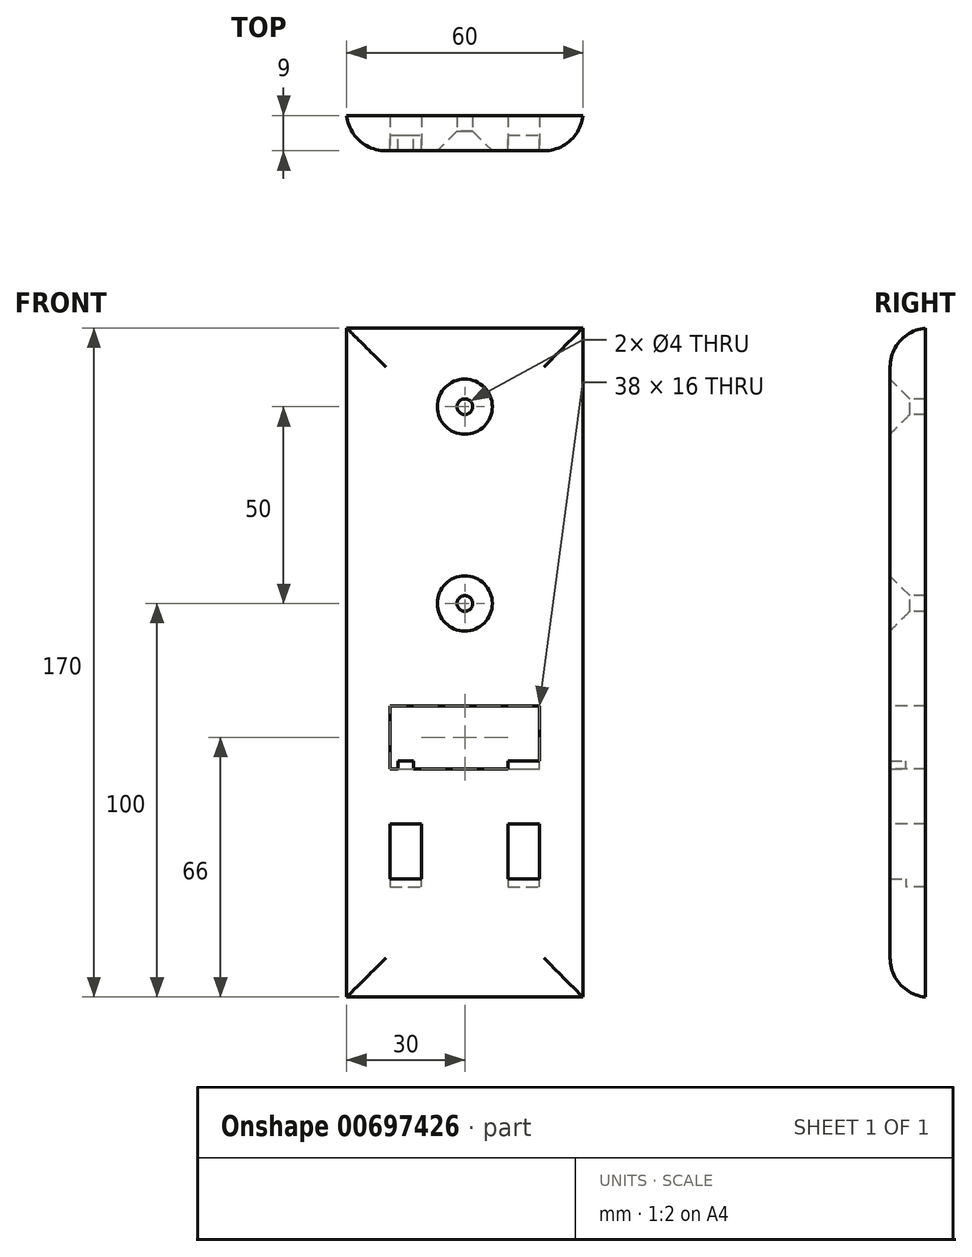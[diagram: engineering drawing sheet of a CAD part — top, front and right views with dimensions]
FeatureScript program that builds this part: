
annotation { "Feature Type Name" : "Feature", "Feature Type Description" : "" }
export const myFeature = defineFeature(function(context is Context, id is Id, definition is map)
    precondition{}
    {
        {
            var Q0;
            Q0=qCreatedBy(makeId("Front.planeOp"),FACE);
            var sketch = newSketch(context, id + "F0", { "sketchPlane" : qUnion([Q0])});
            skLineSegment(sketch, "E0", {"start": v(0, 0) * mm, "end": v(-30, 0) * mm});
            skLineSegment(sketch, "E1", {"start": v(-30, 0) * mm, "end": v(30, 0) * mm});
            skLineSegment(sketch, "E2", {"start": v(30, 0) * mm, "end": v(30, 80) * mm});
            skLineSegment(sketch, "E3", {"start": v(30, 80) * mm, "end": v(-30, 80) * mm});
            skLineSegment(sketch, "E4", {"start": v(-30, 80) * mm, "end": v(-30, 0) * mm});
            skLineSegment(sketch, "E5", {"start": v(-30, 0) * mm, "end": v(-30, 50) * mm, "construction": true});
            skLineSegment(sketch, "E6", {"start": v(-30, 50) * mm, "end": v(30, 50) * mm, "construction": true});
            skLineSegment(sketch, "E7", {"start": v(30, 50) * mm, "end": v(0, 50) * mm, "construction": true});
            skLineSegment(sketch, "E8", {"start": v(0, 50) * mm, "end": v(0, 20) * mm, "construction": true});
            skLineSegment(sketch, "E9", {"start": v(0, 20) * mm, "end": v(30, 20) * mm, "construction": true});
            skLineSegment(sketch, "E10", {"start": v(30, 20) * mm, "end": v(-30, 20) * mm, "construction": true});
            skPoint(sketch, "E10.endSnap0", {"position": v(15, 20) * mm});
            skLineSegment(sketch, "E11.bottom", {"start": v(15, 50) * mm, "end": v(-15, 50) * mm, "construction": true});
            skLineSegment(sketch, "E11.top", {"start": v(15, 20) * mm, "end": v(-15, 20) * mm, "construction": true});
            skLineSegment(sketch, "E11.left", {"start": v(15, 50) * mm, "end": v(15, 20) * mm, "construction": true});
            skLineSegment(sketch, "E11.right", {"start": v(-15, 50) * mm, "end": v(-15, 20) * mm, "construction": true});
            skPoint(sketch, "E11.middle", {"position": v(0, 35) * mm});
            skLineSegment(sketch, "E12", {"start": v(-15, 50) * mm, "end": v(15, 20) * mm, "construction": true});
            skLineSegment(sketch, "E13", {"start": v(15, 50) * mm, "end": v(-15, 20) * mm, "construction": true});
            skLineSegment(sketch, "E14.bottom", {"start": v(-11, 46) * mm, "end": v(-19, 46) * mm});
            skLineSegment(sketch, "E14.top", {"start": v(-11, 54) * mm, "end": v(-19, 54) * mm});
            skLineSegment(sketch, "E14.left", {"start": v(-11, 46) * mm, "end": v(-11, 54) * mm});
            skLineSegment(sketch, "E14.right", {"start": v(-19, 46) * mm, "end": v(-19, 54) * mm});
            skPoint(sketch, "E14.middle", {"position": v(-15, 50) * mm});
            skLineSegment(sketch, "E15.bottom", {"start": v(19, 46) * mm, "end": v(11, 46) * mm});
            skLineSegment(sketch, "E15.top", {"start": v(19, 54) * mm, "end": v(11, 54) * mm});
            skLineSegment(sketch, "E15.left", {"start": v(19, 46) * mm, "end": v(19, 54) * mm});
            skLineSegment(sketch, "E15.right", {"start": v(11, 46) * mm, "end": v(11, 54) * mm});
            skPoint(sketch, "E15.middle", {"position": v(15, 50) * mm});
            skLineSegment(sketch, "E16.bottom", {"start": v(-11, 16) * mm, "end": v(-19, 16) * mm});
            skLineSegment(sketch, "E16.top", {"start": v(-11, 24) * mm, "end": v(-19, 24) * mm});
            skLineSegment(sketch, "E16.left", {"start": v(-11, 16) * mm, "end": v(-11, 24) * mm});
            skLineSegment(sketch, "E16.right", {"start": v(-19, 16) * mm, "end": v(-19, 24) * mm});
            skPoint(sketch, "E16.middle", {"position": v(-15, 20) * mm});
            skLineSegment(sketch, "E17.bottom", {"start": v(19, 16) * mm, "end": v(11, 16) * mm});
            skLineSegment(sketch, "E17.top", {"start": v(19, 24) * mm, "end": v(11, 24) * mm});
            skLineSegment(sketch, "E17.left", {"start": v(19, 16) * mm, "end": v(19, 24) * mm});
            skLineSegment(sketch, "E17.right", {"start": v(11, 16) * mm, "end": v(11, 24) * mm});
            skLineSegment(sketch, "E18.bottom", {"start": v(-19, 46) * mm, "end": v(-11, 46) * mm});
            skLineSegment(sketch, "E18.left", {"start": v(-19, 46) * mm, "end": v(-19, 48) * mm});
            skLineSegment(sketch, "E18.right", {"start": v(-11, 46) * mm, "end": v(-11, 48) * mm});
            skLineSegment(sketch, "E19.top", {"start": v(-19, 38) * mm, "end": v(-11, 38) * mm});
            skLineSegment(sketch, "E19.left", {"start": v(-19, 46) * mm, "end": v(-19, 38) * mm});
            skLineSegment(sketch, "E19.right", {"start": v(-11, 46) * mm, "end": v(-11, 38) * mm});
            skLineSegment(sketch, "E20.bottom", {"start": v(11, 46) * mm, "end": v(19, 46) * mm});
            skLineSegment(sketch, "E20.top", {"start": v(11, 38) * mm, "end": v(19, 38) * mm});
            skLineSegment(sketch, "E20.left", {"start": v(11, 46) * mm, "end": v(11, 38) * mm});
            skLineSegment(sketch, "E20.right", {"start": v(19, 46) * mm, "end": v(19, 38) * mm});
            skLineSegment(sketch, "E21.bottom", {"start": v(-19, 16) * mm, "end": v(-11, 16) * mm});
            skLineSegment(sketch, "E21.top", {"start": v(-19, 8) * mm, "end": v(-11, 8) * mm});
            skLineSegment(sketch, "E21.left", {"start": v(-19, 16) * mm, "end": v(-19, 8) * mm});
            skLineSegment(sketch, "E21.right", {"start": v(-11, 16) * mm, "end": v(-11, 8) * mm});
            skLineSegment(sketch, "E22.bottom", {"start": v(11, 16) * mm, "end": v(19, 16) * mm});
            skLineSegment(sketch, "E22.top", {"start": v(11, 8) * mm, "end": v(19, 8) * mm});
            skLineSegment(sketch, "E22.left", {"start": v(11, 16) * mm, "end": v(11, 8) * mm});
            skLineSegment(sketch, "E22.right", {"start": v(19, 16) * mm, "end": v(19, 8) * mm});
            skLineSegment(sketch, "E23.bottom", {"start": v(-19, 46) * mm, "end": v(-17, 46) * mm});
            skLineSegment(sketch, "E23.top", {"start": v(-19, 38) * mm, "end": v(-17, 38) * mm});
            skLineSegment(sketch, "E23.right", {"start": v(-17, 46) * mm, "end": v(-17, 38) * mm});
            skLineSegment(sketch, "E24.bottom", {"start": v(-11, 46) * mm, "end": v(-13, 46) * mm});
            skLineSegment(sketch, "E24.top", {"start": v(-11, 38) * mm, "end": v(-13, 38) * mm});
            skLineSegment(sketch, "E24.right", {"start": v(-13, 46) * mm, "end": v(-13, 38) * mm});
            skLineSegment(sketch, "E25.bottom", {"start": v(11, 46) * mm, "end": v(13, 46) * mm});
            skLineSegment(sketch, "E25.top", {"start": v(11, 38) * mm, "end": v(13, 38) * mm});
            skLineSegment(sketch, "E25.right", {"start": v(13, 46) * mm, "end": v(13, 38) * mm});
            skLineSegment(sketch, "E26.bottom", {"start": v(19, 46) * mm, "end": v(17, 46) * mm});
            skLineSegment(sketch, "E26.top", {"start": v(19, 38) * mm, "end": v(17, 38) * mm});
            skLineSegment(sketch, "E26.right", {"start": v(17, 46) * mm, "end": v(17, 38) * mm});
            skLineSegment(sketch, "E27.bottom", {"start": v(19, 16) * mm, "end": v(17, 16) * mm});
            skLineSegment(sketch, "E27.top", {"start": v(19, 8) * mm, "end": v(17, 8) * mm});
            skLineSegment(sketch, "E28.bottom", {"start": v(-11, 16) * mm, "end": v(-13, 16) * mm});
            skLineSegment(sketch, "E28.top", {"start": v(-11, 8) * mm, "end": v(-13, 8) * mm});
            skLineSegment(sketch, "E28.right", {"start": v(-13, 16) * mm, "end": v(-13, 8) * mm});
            skLineSegment(sketch, "E29.right", {"start": v(17, 16) * mm, "end": v(17, 8) * mm});
            skLineSegment(sketch, "E30.bottom", {"start": v(11, 16) * mm, "end": v(13, 16) * mm});
            skLineSegment(sketch, "E30.top", {"start": v(11, 8) * mm, "end": v(13, 8) * mm});
            skLineSegment(sketch, "E30.right", {"start": v(13, 16) * mm, "end": v(13, 8) * mm});
            skLineSegment(sketch, "E31.bottom", {"start": v(-19, 16) * mm, "end": v(-17, 16) * mm});
            skLineSegment(sketch, "E31.top", {"start": v(-19, 8) * mm, "end": v(-17, 8) * mm});
            skLineSegment(sketch, "E31.right", {"start": v(-17, 16) * mm, "end": v(-17, 8) * mm});
            skLineSegment(sketch, "E32.top", {"start": v(-19, 40) * mm, "end": v(-11, 40) * mm});
            skLineSegment(sketch, "E32.left", {"start": v(-19, 38) * mm, "end": v(-19, 40) * mm});
            skLineSegment(sketch, "E32.right", {"start": v(-11, 38) * mm, "end": v(-11, 40) * mm});
            skLineSegment(sketch, "E33", {"start": v(11, 40) * mm, "end": v(19, 40) * mm});
            skLineSegment(sketch, "E34", {"start": v(-11, 10) * mm, "end": v(-19, 10) * mm});
            skLineSegment(sketch, "E35", {"start": v(11, 10) * mm, "end": v(19, 10) * mm});
            skLineSegment(sketch, "E36.top", {"start": v(-30, 150) * mm, "end": v(30, 150) * mm});
            skLineSegment(sketch, "E36.left", {"start": v(-30, 0) * mm, "end": v(-30, 150) * mm});
            skLineSegment(sketch, "E36.right", {"start": v(30, 0) * mm, "end": v(30, 150) * mm});
            skLineSegment(sketch, "E37", {"start": v(0, 150) * mm, "end": v(0, 80) * mm, "construction": true});
            skLineSegment(sketch, "E38", {"start": v(0, 80) * mm, "end": v(0, 50) * mm, "construction": true});
            skLineSegment(sketch, "E39", {"start": v(0, 150) * mm, "end": v(0, 130) * mm, "construction": true});
            skLineSegment(sketch, "E40", {"start": v(0, 130) * mm, "end": v(0, 80) * mm, "construction": true});
            skCircle(sketch, "E41", {"center": v(0, 130) * mm, "radius": 2 * mm});
            skCircle(sketch, "E42", {"center": v(0, 80) * mm, "radius": 2 * mm});
            skLineSegment(sketch, "E43", {"start": v(-11, 54) * mm, "end": v(11, 54) * mm});
            skLineSegment(sketch, "E44", {"start": v(11, 40) * mm, "end": v(-11, 40) * mm});
            skLineSegment(sketch, "E45", {"start": v(11, 38) * mm, "end": v(-11, 38) * mm});
            skLineSegment(sketch, "E46", {"start": v(-30, 0) * mm, "end": v(-30, -20) * mm});
            skLineSegment(sketch, "E47", {"start": v(-30, -20) * mm, "end": v(30, -20) * mm});
            skLineSegment(sketch, "E48", {"start": v(30, -20) * mm, "end": v(30, 0) * mm});
            skSolve(sketch);
        }
        {
            var Q0;
            {var subQ3=sQuery(id+"F0.wireOp",EDGE,"E36.top");Q0=makeQuery(id+"F0.imprint","IMPRINT",FACE,{"disambiguationData":[TD([[makeQuery(id+"F0.imprint","IMPRINT",EDGE,{"derivedFrom":subQ3}),-1.0]])]});}
            var Q1;
            Q1=makeQuery(id+"F0.imprint","IMPRINT",FACE,{"disambiguationData":[TD([[makeQuery(id+"F0.imprint","IMPRINT",EDGE,{"derivedFrom":sQuery(id+"F0.wireOp",EDGE,"E14.top")}),-1.0]])]});
            var Q2;
            {var subQ0=sQuery(id+"F0.wireOp",EDGE,"E46");Q2=makeQuery(id+"F0.imprint","IMPRINT",FACE,{"disambiguationData":[TD([[makeQuery(id+"F0.imprint","IMPRINT",EDGE,{"derivedFrom":subQ0}),1.0]])]});}
            extrude(context, id + "F1", {"entities" : qUnion([Q0, Q1, Q2]), "oppositeDirection" : true, "depth" : 5 * mm, "offsetDistance" : 25 * mm});
        }
        {
            var Q0;
            {var subQ0=sQuery(id+"F0.wireOp",EDGE,"E23.bottom");Q0=makeQuery(id+"F0.imprint","IMPRINT",FACE,{"disambiguationData":[TD([[makeQuery(id+"F0.imprint","IMPRINT",EDGE,{"derivedFrom":subQ0}),-1.0]])]});}
            var Q1;
            {var subQ5=sQuery(id+"F0.wireOp",EDGE,"E32.left");Q1=makeQuery(id+"F0.imprint","IMPRINT",FACE,{"disambiguationData":[TD([[makeQuery(id+"F0.imprint","IMPRINT",EDGE,{"derivedFrom":subQ5}),-1.0]])]});}
            var Q2;
            {var subQ0=sQuery(id+"F0.wireOp",EDGE,"E19.top");var subQ1=sQuery(id+"F0.wireOp",EDGE,"E23.right");var subQ2=makeQuery(id+"F0.imprint","INTERSECT",VERTEX,{"derivedFrom":[subQ1,subQ0]});Q2=makeQuery(id+"F0.imprint","IMPRINT",FACE,{"disambiguationData":[TD([[makeQuery(id+"F0.imprint","IMPRINT",EDGE,{"disambiguationData":[TD([[subQ2,1.0]])],"derivedFrom":subQ1}),1.0]])]});}
            var Q3;
            {var subQ5=sQuery(id+"F0.wireOp",EDGE,"E32.right");Q3=makeQuery(id+"F0.imprint","IMPRINT",FACE,{"disambiguationData":[TD([[makeQuery(id+"F0.imprint","IMPRINT",EDGE,{"derivedFrom":subQ5}),1.0]])]});}
            var Q4;
            {var subQ0=sQuery(id+"F0.wireOp",EDGE,"E25.top");Q4=makeQuery(id+"F0.imprint","IMPRINT",FACE,{"disambiguationData":[TD([[makeQuery(id+"F0.imprint","IMPRINT",EDGE,{"derivedFrom":subQ0}),1.0]])]});}
            var Q5;
            {var subQ0=sQuery(id+"F0.wireOp",EDGE,"E20.top");Q5=makeQuery(id+"F0.imprint","IMPRINT",FACE,{"disambiguationData":[TD([[makeQuery(id+"F0.imprint","IMPRINT",EDGE,{"derivedFrom":subQ0}),1.0]])]});}
            var Q6;
            {var subQ0=sQuery(id+"F0.wireOp",EDGE,"E26.top");Q6=makeQuery(id+"F0.imprint","IMPRINT",FACE,{"disambiguationData":[TD([[makeQuery(id+"F0.imprint","IMPRINT",EDGE,{"derivedFrom":subQ0}),-1.0]])]});}
            var Q7;
            {var subQ0=sQuery(id+"F0.wireOp",EDGE,"E26.bottom");Q7=makeQuery(id+"F0.imprint","IMPRINT",FACE,{"disambiguationData":[TD([[makeQuery(id+"F0.imprint","IMPRINT",EDGE,{"derivedFrom":subQ0}),1.0]])]});}
            var Q8;
            {var subQ0=sQuery(id+"F0.wireOp",EDGE,"NN5jano5-v2yu-koeT-qmYi-EJZCYhMvK6H8.bottom");Q8=makeQuery(id+"F0.imprint","IMPRINT",FACE,{"disambiguationData":[TD([[makeQuery(id+"F0.imprint","IMPRINT",EDGE,{"derivedFrom":subQ0}),-1.0]])]});}
            var Q9;
            {var subQ0=sQuery(id+"F0.wireOp",EDGE,"NN5jano5-v2yu-koeT-qmYi-EJZCYhMvK6H8.top");Q9=makeQuery(id+"F0.imprint","IMPRINT",FACE,{"disambiguationData":[TD([[makeQuery(id+"F0.imprint","IMPRINT",EDGE,{"derivedFrom":subQ0}),1.0]])]});}
            var Q10;
            {var subQ0=sQuery(id+"F0.wireOp",EDGE,"EvVcPynJ-Of4R-KM36-nz1v-TSqms22A6YGf.top");Q10=makeQuery(id+"F0.imprint","IMPRINT",FACE,{"disambiguationData":[TD([[makeQuery(id+"F0.imprint","IMPRINT",EDGE,{"derivedFrom":subQ0}),1.0]])]});}
            var Q11;
            {var subQ0=sQuery(id+"F0.wireOp",EDGE,"xoLzNPPj-sGxH-p6tm-CG6E-vPTKjg17kD3K.top");Q11=makeQuery(id+"F0.imprint","IMPRINT",FACE,{"disambiguationData":[TD([[makeQuery(id+"F0.imprint","IMPRINT",EDGE,{"derivedFrom":subQ0}),1.0]])]});}
            var Q12;
            {var subQ0=sQuery(id+"F0.wireOp",EDGE,"xoLzNPPj-sGxH-p6tm-CG6E-vPTKjg17kD3K.bottom");Q12=makeQuery(id+"F0.imprint","IMPRINT",FACE,{"disambiguationData":[TD([[makeQuery(id+"F0.imprint","IMPRINT",EDGE,{"derivedFrom":subQ0}),-1.0]])]});}
            var Q13;
            {var subQ0=sQuery(id+"F0.wireOp",EDGE,"E31.bottom");Q13=makeQuery(id+"F0.imprint","IMPRINT",FACE,{"disambiguationData":[TD([[makeQuery(id+"F0.imprint","IMPRINT",EDGE,{"derivedFrom":subQ0}),-1.0]])]});}
            var Q14;
            {var subQ0=sQuery(id+"F0.wireOp",EDGE,"E31.top");Q14=makeQuery(id+"F0.imprint","IMPRINT",FACE,{"disambiguationData":[TD([[makeQuery(id+"F0.imprint","IMPRINT",EDGE,{"derivedFrom":subQ0}),1.0]])]});}
            var Q15;
            {var subQ0=sQuery(id+"F0.wireOp",EDGE,"E21.top");Q15=makeQuery(id+"F0.imprint","IMPRINT",FACE,{"disambiguationData":[TD([[makeQuery(id+"F0.imprint","IMPRINT",EDGE,{"derivedFrom":subQ0}),1.0]])]});}
            var Q16;
            {var subQ0=sQuery(id+"F0.wireOp",EDGE,"E28.top");Q16=makeQuery(id+"F0.imprint","IMPRINT",FACE,{"disambiguationData":[TD([[makeQuery(id+"F0.imprint","IMPRINT",EDGE,{"derivedFrom":subQ0}),-1.0]])]});}
            var Q17;
            {var subQ0=sQuery(id+"F0.wireOp",EDGE,"E28.bottom");Q17=makeQuery(id+"F0.imprint","IMPRINT",FACE,{"disambiguationData":[TD([[makeQuery(id+"F0.imprint","IMPRINT",EDGE,{"derivedFrom":subQ0}),1.0]])]});}
            var Q18;
            {var subQ0=sQuery(id+"F0.wireOp",EDGE,"E30.bottom");Q18=makeQuery(id+"F0.imprint","IMPRINT",FACE,{"disambiguationData":[TD([[makeQuery(id+"F0.imprint","IMPRINT",EDGE,{"derivedFrom":subQ0}),-1.0]])]});}
            var Q19;
            {var subQ0=sQuery(id+"F0.wireOp",EDGE,"E30.top");Q19=makeQuery(id+"F0.imprint","IMPRINT",FACE,{"disambiguationData":[TD([[makeQuery(id+"F0.imprint","IMPRINT",EDGE,{"derivedFrom":subQ0}),1.0]])]});}
            var Q20;
            {var subQ0=sQuery(id+"F0.wireOp",EDGE,"E27.bottom");Q20=makeQuery(id+"F0.imprint","IMPRINT",FACE,{"disambiguationData":[TD([[makeQuery(id+"F0.imprint","IMPRINT",EDGE,{"derivedFrom":subQ0}),1.0]])]});}
            var Q21;
            {var subQ0=sQuery(id+"F0.wireOp",EDGE,"E22.top");Q21=makeQuery(id+"F0.imprint","IMPRINT",FACE,{"disambiguationData":[TD([[makeQuery(id+"F0.imprint","IMPRINT",EDGE,{"derivedFrom":subQ0}),1.0]])]});}
            var Q22;
            {var subQ0=sQuery(id+"F0.wireOp",EDGE,"E27.top");Q22=makeQuery(id+"F0.imprint","IMPRINT",FACE,{"disambiguationData":[TD([[makeQuery(id+"F0.imprint","IMPRINT",EDGE,{"derivedFrom":subQ0}),-1.0]])]});}
            var Q23;
            Q23=makeQuery(id+"F0.imprint","IMPRINT",FACE,{"disambiguationData":[TD([[makeQuery(id+"F0.imprint","IMPRINT",EDGE,{"derivedFrom":sQuery(id+"F0.wireOp",EDGE,"E14.top")}),-1.0]])]});
            var Q24;
            {var subQ3=sQuery(id+"F0.wireOp",EDGE,"E36.top");Q24=makeQuery(id+"F0.imprint","IMPRINT",FACE,{"disambiguationData":[TD([[makeQuery(id+"F0.imprint","IMPRINT",EDGE,{"derivedFrom":subQ3}),-1.0]])]});}
            var Q25;
            Q25=makeQuery(id+"F0.imprint","IMPRINT",FACE,{"disambiguationData":[TD([[makeQuery(id+"F0.imprint","IMPRINT",EDGE,{"derivedFrom":sQuery(id+"F0.wireOp",EDGE,"E32.right")}),-1.0]])]});
            var Q26;
            {var subQ0=sQuery(id+"F0.wireOp",EDGE,"E46");Q26=makeQuery(id+"F0.imprint","IMPRINT",FACE,{"disambiguationData":[TD([[makeQuery(id+"F0.imprint","IMPRINT",EDGE,{"derivedFrom":subQ0}),1.0]])]});}
            extrude(context, id + "F2", {"entities" : qUnion([Q0, Q1, Q2, Q3, Q4, Q5, Q6, Q7, Q8, Q9, Q10, Q11, Q12, Q13, Q14, Q15, Q16, Q17, Q18, Q19, Q20, Q21, Q22, Q23, Q24, Q25, Q26]), "operationType" : NewBodyOperationType.ADD, "depth" : 4 * mm, "offsetDistance" : 25 * mm});
        }
        {
            var Q0;
            Q0=makeQuery(id+"F2.opExtrude","CAP_EDGE",EDGE,{"disambiguationData":[OSD([sQuery(id+"F0.wireOp",EDGE,"E41")])],"isStart":false});
            var Q1;
            Q1=makeQuery(id+"F2.opExtrude","CAP_EDGE",EDGE,{"disambiguationData":[OSD([sQuery(id+"F0.wireOp",EDGE,"E42")])],"isStart":false});
            chamfer(context, id + "F3", {"entities" : qUnion([Q0, Q1]), "width" : 5 * mm, "tangentPropagation" : true});
        }
        {
            var Q0;
            Q0=makeQuery(id+"F2.opExtrude","CAP_EDGE",EDGE,{"disambiguationData":[OSD([sQuery(id+"F0.wireOp",EDGE,"E1")])],"isStart":false});
            var Q1;
            Q1=makeQuery(id+"F2.opExtrude","CAP_EDGE",EDGE,{"disambiguationData":[OSD([sQuery(id+"F0.wireOp",EDGE,"E36.left")])],"isStart":false});
            var Q2;
            Q2=makeQuery(id+"F2.opExtrude","CAP_EDGE",EDGE,{"disambiguationData":[OSD([sQuery(id+"F0.wireOp",EDGE,"E36.right")])],"isStart":false});
            var Q3;
            Q3=makeQuery(id+"F2.opExtrude","CAP_EDGE",EDGE,{"disambiguationData":[OSD([sQuery(id+"F0.wireOp",EDGE,"E36.top")])],"isStart":false});
            var Q4;
            Q4=makeQuery(id+"F2.opExtrude","CAP_EDGE",EDGE,{"disambiguationData":[OSD([sQuery(id+"F0.wireOp",EDGE,"E47")])],"isStart":false});
            fillet(context, id + "F4", {"entities" : qUnion([Q0, Q1, Q2, Q3, Q4]), "radius" : 10 * mm, "tangentPropagation" : true, "allowEdgeOverflow" : false});
        }
    });
